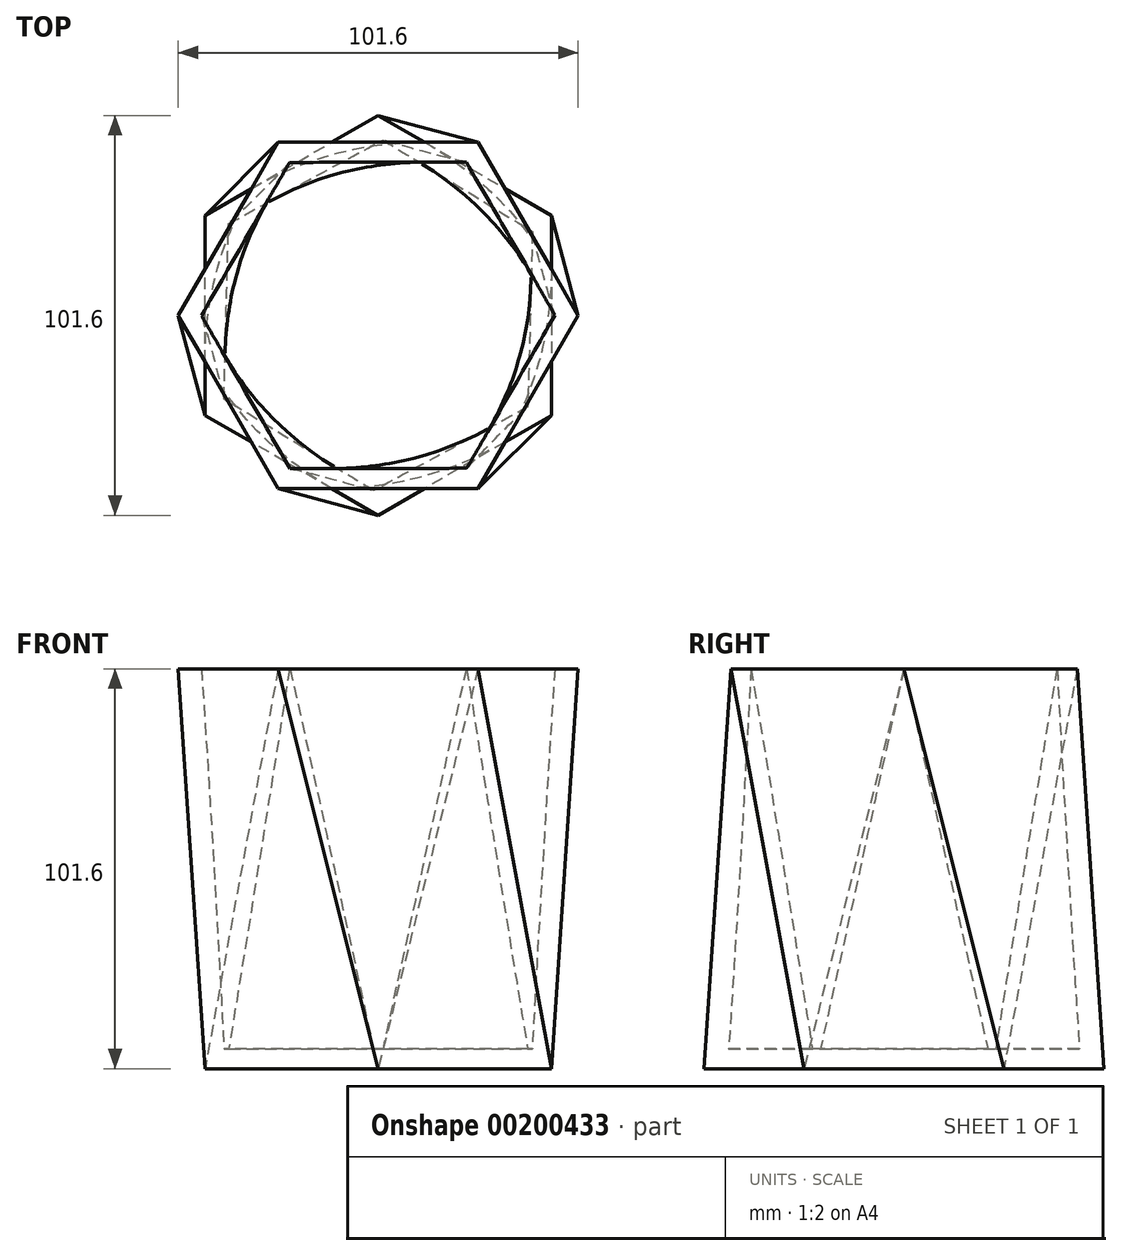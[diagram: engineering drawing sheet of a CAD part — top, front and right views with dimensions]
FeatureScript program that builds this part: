
annotation { "Feature Type Name" : "Feature", "Feature Type Description" : "" }
export const myFeature = defineFeature(function(context is Context, id is Id, definition is map)
    precondition{}
    {
        {
            var Q0;
            Q0=qCreatedBy(makeId("Top.planeOp"),FACE);
            var sketch = newSketch(context, id + "F0", { "sketchPlane" : qUnion([Q0])});
            skCircle(sketch, "E0.cCircle", {"center": v(0, 0) * mm, "radius": 44 * mm, "construction": true});
            skLineSegment(sketch, "E0.0", {"start": v(-44, -25.4) * mm, "end": v(-44, 25.4) * mm});
            skLineSegment(sketch, "E0.1", {"start": v(-44, 25.4) * mm, "end": v(0, 50.8) * mm});
            skLineSegment(sketch, "E0.2", {"start": v(0, 50.8) * mm, "end": v(44, 25.4) * mm});
            skLineSegment(sketch, "E0.3", {"start": v(44, 25.4) * mm, "end": v(44, -25.4) * mm});
            skLineSegment(sketch, "E0.4", {"start": v(44, -25.4) * mm, "end": v(0, -50.8) * mm});
            skLineSegment(sketch, "E0.5", {"start": v(0, -50.8) * mm, "end": v(-44, -25.4) * mm});
            skPoint(sketch, "E0.0.midPoint", {"position": v(-44, 0) * mm});
            skSolve(sketch);
        }
        {
            var Q0;
            Q0=qCreatedBy(makeId("Top.planeOp"),FACE);
            cPlane(context, id + "F1", {"entities" : qUnion([Q0]), "cplaneType" : CPlaneType.OFFSET, "offset" : 101.6 * mm, "width" : 152.4 * mm, "height" : 152.4 * mm});
        }
        {
            var Q0;
            Q0=qCreatedBy(id+"F1.planeOp",FACE);
            var sketch = newSketch(context, id + "F2", { "sketchPlane" : qUnion([Q0])});
            skCircle(sketch, "E1.cCircle", {"center": v(0, 0) * mm, "radius": 44 * mm, "construction": true});
            skLineSegment(sketch, "E1.0", {"start": v(-25.4, 44) * mm, "end": v(25.4, 44) * mm});
            skLineSegment(sketch, "E1.1", {"start": v(25.4, 44) * mm, "end": v(50.8, 0) * mm});
            skLineSegment(sketch, "E1.2", {"start": v(50.8, 0) * mm, "end": v(25.4, -44) * mm});
            skLineSegment(sketch, "E1.3", {"start": v(25.4, -44) * mm, "end": v(-25.4, -44) * mm});
            skLineSegment(sketch, "E1.4", {"start": v(-25.4, -44) * mm, "end": v(-50.8, 0) * mm});
            skLineSegment(sketch, "E1.5", {"start": v(-50.8, 0) * mm, "end": v(-25.4, 44) * mm});
            skPoint(sketch, "E1.0.midPoint", {"position": v(0, 44) * mm});
            skSolve(sketch);
        }
        {
            var Q0;
            Q0=makeQuery(id+"F2.imprint","IMPRINT",FACE,{"disambiguationData":[TD([[makeQuery(id+"F2.imprint","IMPRINT",EDGE,{"derivedFrom":sQuery(id+"F2.wireOp",EDGE,"E1.0")}),-1.0]])]});
            var Q1;
            Q1=makeQuery(id+"F0.imprint","IMPRINT",FACE,{"disambiguationData":[TD([[makeQuery(id+"F0.imprint","IMPRINT",EDGE,{"derivedFrom":sQuery(id+"F0.wireOp",EDGE,"E0.0")}),-1.0]])]});
            loft(context, id + "F3", {"sheetProfilesArray" : [{ "sheetProfileEntities" : qUnion([Q0]) }, { "sheetProfileEntities" : qUnion([Q1]) }]});
        }
        {
            var Q0;
            Q0=makeQuery(id+"F3.opLoft","CAP_FACE",FACE,{"disambiguationData":[OSD([makeQuery(id+"F2.imprint","IMPRINT",FACE,{"disambiguationData":[TD([[makeQuery(id+"F2.imprint","IMPRINT",EDGE,{"derivedFrom":sQuery(id+"F2.wireOp",EDGE,"E1.0")}),-1.0]])]})])],"isStart":true});
            shell(context, id + "F4", {"entities" : qUnion([Q0]), "thickness" : 5.08 * mm});
        }
    });
